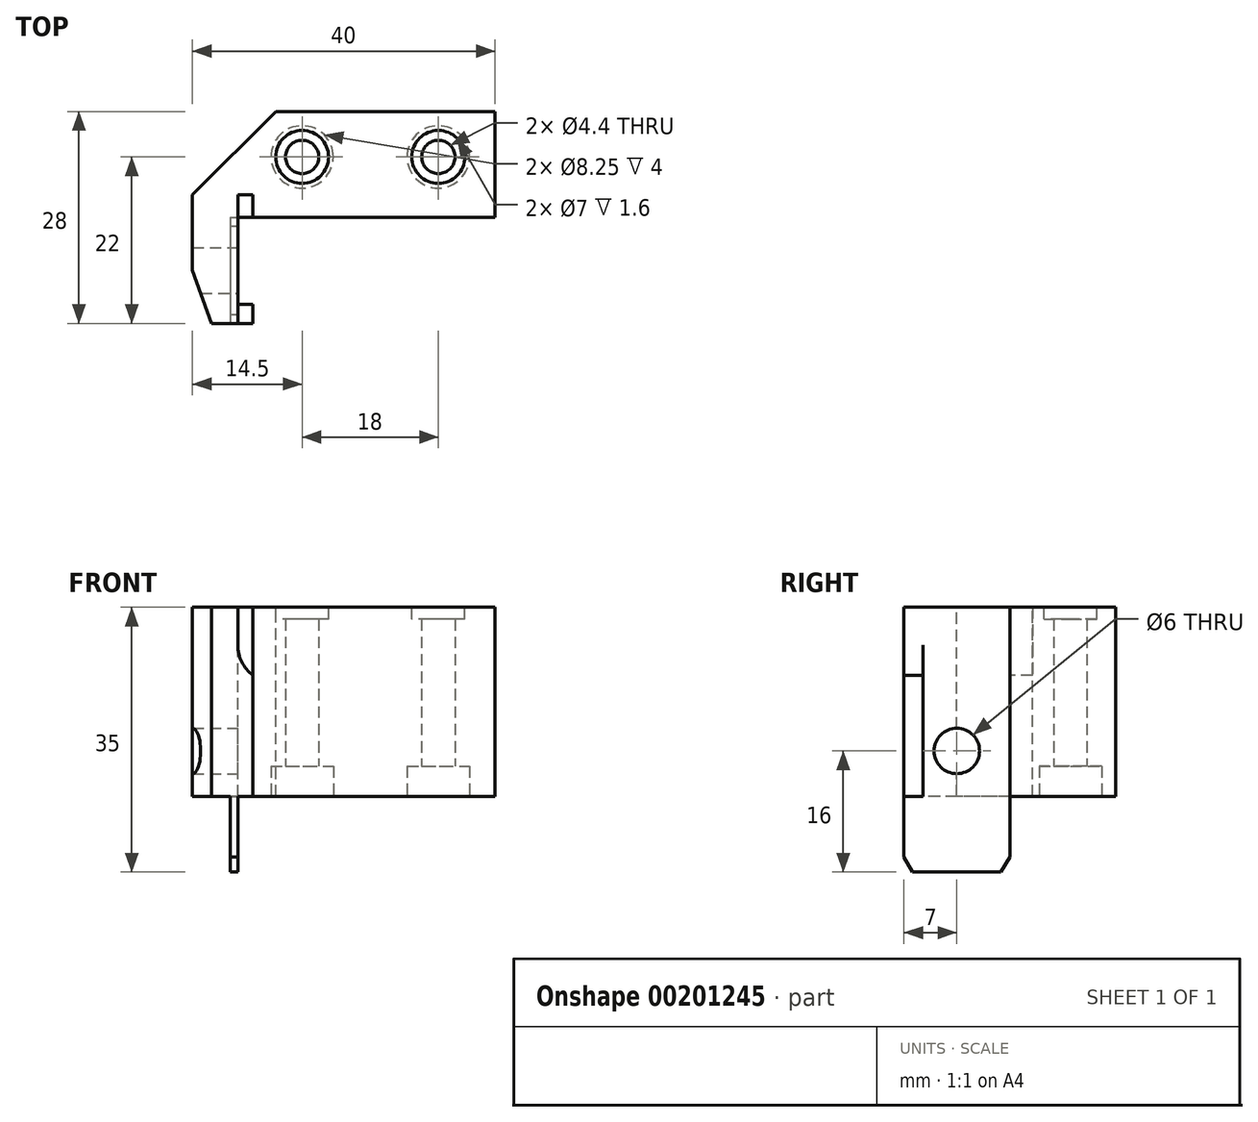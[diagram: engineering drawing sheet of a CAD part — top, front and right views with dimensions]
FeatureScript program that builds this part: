
annotation { "Feature Type Name" : "Feature", "Feature Type Description" : "" }
export const myFeature = defineFeature(function(context is Context, id is Id, definition is map)
    precondition{}
    {
        {
            var Q0;
            Q0=qCreatedBy(makeId("Top.planeOp"),FACE);
            var sketch = newSketch(context, id + "F0", { "sketchPlane" : qUnion([Q0])});
            skLineSegment(sketch, "E0", {"start": v(0, 14) * mm, "end": v(0, 28) * mm});
            skLineSegment(sketch, "E1", {"start": v(0, 28) * mm, "end": v(-29, 28) * mm});
            skLineSegment(sketch, "E2", {"start": v(-29, 28) * mm, "end": v(-40, 17) * mm});
            skLineSegment(sketch, "E3", {"start": v(-40, 17) * mm, "end": v(-40, 7) * mm});
            skLineSegment(sketch, "E4", {"start": v(-40, 7) * mm, "end": v(-37.45, 0) * mm});
            skLineSegment(sketch, "E5", {"start": v(-37.45, 0) * mm, "end": v(-32, 0) * mm});
            skLineSegment(sketch, "E6", {"start": v(-32, 0) * mm, "end": v(-32, 2.5) * mm});
            skLineSegment(sketch, "E7", {"start": v(-32, 2.5) * mm, "end": v(-34, 2.5) * mm});
            skLineSegment(sketch, "E8", {"start": v(-34, 2.5) * mm, "end": v(-34, 14) * mm});
            skLineSegment(sketch, "E9", {"start": v(-34, 14) * mm, "end": v(0, 14) * mm});
            skLineSegment(sketch, "E10", {"start": v(0, 22) * mm, "end": v(-35, 22) * mm, "construction": true});
            skLineSegment(sketch, "E11", {"start": v(-7.5, 28) * mm, "end": v(-7.5, 14) * mm, "construction": true});
            skLineSegment(sketch, "E12", {"start": v(-25.5, 14) * mm, "end": v(-25.5, 28) * mm, "construction": true});
            skPoint(sketch, "E13", {"position": v(-25.5, 22) * mm});
            skPoint(sketch, "E14", {"position": v(-7.5, 22) * mm});
            skSolve(sketch);
        }
        {
            var Q0;
            Q0=makeQuery(id+"F0.imprint","IMPRINT",FACE,{"disambiguationData":[TD([[makeQuery(id+"F0.imprint","IMPRINT",EDGE,{"derivedFrom":sQuery(id+"F0.wireOp",EDGE,"E0")}),1.0]])]});
            extrude(context, id + "F1", {"entities" : qUnion([Q0]), "oppositeDirection" : true, "depth" : 35 * mm});
        }
        {
            var Q0;
            Q0=makeQuery(id+"F1.opExtrude","SWEPT_FACE",FACE,{"disambiguationData":[OSD([sQuery(id+"F0.wireOp",EDGE,"E5")])]});
            var sketch = newSketch(context, id + "F2", { "sketchPlane" : qUnion([Q0])});
            skLineSegment(sketch, "E15.0", {"start": v(-34, 0) * mm, "end": v(0, 0) * mm});
            skLineSegment(sketch, "E16.0", {"start": v(0, -35) * mm, "end": v(0, 0) * mm});
            skLineSegment(sketch, "E17.0", {"start": v(-34, -35) * mm, "end": v(0, -35) * mm});
            skLineSegment(sketch, "E18.0", {"start": v(-37.45, -35) * mm, "end": v(-32, -35) * mm});
            skLineSegment(sketch, "E19.0", {"start": v(-40, -35) * mm, "end": v(-37.45, -35) * mm});
            skLineSegment(sketch, "E20.0", {"start": v(-40, -35) * mm, "end": v(-40, 0) * mm});
            skLineSegment(sketch, "E21.0", {"start": v(-40, 0) * mm, "end": v(-37.45, 0) * mm});
            skLineSegment(sketch, "E22.0", {"start": v(-37.45, 0) * mm, "end": v(-32, 0) * mm});
            skLineSegment(sketch, "E23.0", {"start": v(-32, -35) * mm, "end": v(-32, 0) * mm});
            skLineSegment(sketch, "E24.0", {"start": v(-37.45, -35) * mm, "end": v(-37.45, 0) * mm});
            skLineSegment(sketch, "E25", {"start": v(-34, 0) * mm, "end": v(-34, -5) * mm});
            skLineSegment(sketch, "E26", {"start": v(-29, -10) * mm, "end": v(0, -10) * mm});
            skLineSegment(sketch, "E27", {"start": v(-40, -25) * mm, "end": v(-35, -25) * mm});
            skLineSegment(sketch, "E28", {"start": v(-35, -25) * mm, "end": v(-35, -35) * mm});
            skLineSegment(sketch, "E29", {"start": v(0, -25) * mm, "end": v(-34, -25) * mm});
            skLineSegment(sketch, "E30", {"start": v(-34, -25) * mm, "end": v(-34, -35) * mm});
            skPoint(sketch, "E31.visualSharp", {"position": v(-34, -10) * mm});
            skArc(sketch, "E31.filletArc", {"start": v(-34, -5) * mm, "mid": v(-32.54, -8.54) * mm, "end": v(-29, -10) * mm});
            skSolve(sketch);
        }
        {
            var Q0;
            {var subQ2=sQuery(id+"F2.wireOp",EDGE,"E15.0");Q0=makeQuery(id+"F2.imprint","IMPRINT",FACE,{"disambiguationData":[TD([[makeQuery(id+"F2.imprint","IMPRINT",EDGE,{"derivedFrom":subQ2}),-1.0]])]});}
            var Q1;
            {var subQ3=sQuery(id+"F2.wireOp",EDGE,"E25");Q1=makeQuery(id+"F2.imprint","IMPRINT",FACE,{"disambiguationData":[TD([[makeQuery(id+"F2.imprint","IMPRINT",EDGE,{"derivedFrom":subQ3}),1.0]])]});}
            extrude(context, id + "F3", {"entities" : qUnion([Q0, Q1]), "operationType" : NewBodyOperationType.REMOVE, "oppositeDirection" : true, "depth" : 17 * mm});
        }
        {
            var Q0;
            {var subQ3=sQuery(id+"F2.wireOp",EDGE,"E28");Q0=makeQuery(id+"F2.imprint","IMPRINT",FACE,{"disambiguationData":[TD([[makeQuery(id+"F2.imprint","IMPRINT",EDGE,{"derivedFrom":subQ3}),-1.0]])]});}
            var Q1;
            {var subQ0=sQuery(id+"F2.wireOp",EDGE,"E19.0");Q1=makeQuery(id+"F2.imprint","IMPRINT",FACE,{"disambiguationData":[TD([[makeQuery(id+"F2.imprint","IMPRINT",EDGE,{"derivedFrom":subQ0}),1.0]])]});}
            var Q2;
            {var subQ0=sQuery(id+"F2.wireOp",EDGE,"E17.0");Q2=makeQuery(id+"F2.imprint","IMPRINT",FACE,{"disambiguationData":[TD([[makeQuery(id+"F2.imprint","IMPRINT",EDGE,{"derivedFrom":subQ0}),1.0]])]});}
            extrude(context, id + "F4", {"entities" : qUnion([Q0, Q1, Q2]), "operationType" : NewBodyOperationType.REMOVE, "endBound" : BoundingType.THROUGH_ALL, "oppositeDirection" : true, "depth" : 25 * mm});
        }
        {
            var Q0;
            Q0=makeQuery(id+"F1.opExtrude","SWEPT_FACE",FACE,{"disambiguationData":[OSD([sQuery(id+"F0.wireOp",EDGE,"E1")])]});
            var sketch = newSketch(context, id + "F5", { "sketchPlane" : qUnion([Q0])});
            skLineSegment(sketch, "E32.0", {"start": v(0, -25) * mm, "end": v(34, -25) * mm});
            skLineSegment(sketch, "E33.0", {"start": v(34, -25) * mm, "end": v(34, -35) * mm});
            skLineSegment(sketch, "E34.0", {"start": v(37.45, -35) * mm, "end": v(32, -35) * mm});
            skLineSegment(sketch, "E35.0", {"start": v(32, -35) * mm, "end": v(32, 0) * mm});
            skLineSegment(sketch, "E36.0", {"start": v(35, -25) * mm, "end": v(35, -35) * mm});
            skLineSegment(sketch, "E37.0", {"start": v(40, -25) * mm, "end": v(35, -25) * mm});
            skLineSegment(sketch, "E38.0", {"start": v(40, -35) * mm, "end": v(40, 0) * mm});
            skLineSegment(sketch, "E39.0", {"start": v(37.45, 0) * mm, "end": v(32, 0) * mm});
            skLineSegment(sketch, "E40.0", {"start": v(40, 0) * mm, "end": v(37.45, 0) * mm});
            skLineSegment(sketch, "E41.0", {"start": v(40, -35) * mm, "end": v(37.45, -35) * mm});
            skLineSegment(sketch, "E42", {"start": v(34, -25) * mm, "end": v(35, -25) * mm});
            skSolve(sketch);
        }
        {
            var Q0;
            {var subQ0=sQuery(id+"F5.wireOp",EDGE,"E33.0");Q0=makeQuery(id+"F5.imprint","IMPRINT",FACE,{"disambiguationData":[TD([[makeQuery(id+"F5.imprint","IMPRINT",EDGE,{"derivedFrom":subQ0}),-1.0]])]});}
            var Q1;
            Q1=makeQuery(id+"F1.opExtrude","SWEPT_FACE",FACE,{"disambiguationData":[OSD([sQuery(id+"F0.wireOp",EDGE,"E9")])]});
            extrude(context, id + "F6", {"entities" : qUnion([Q0]), "operationType" : NewBodyOperationType.REMOVE, "endBound" : BoundingType.UP_TO_SURFACE, "oppositeDirection" : true, "endBoundEntityFace" : qUnion([Q1]), "depth" : 25 * mm});
        }
        {
            var Q0;
            Q0=makeQuery(id+"F1.opExtrude","SWEPT_FACE",FACE,{"disambiguationData":[OSD([sQuery(id+"F0.wireOp",EDGE,"E0")])]});
            var sketch = newSketch(context, id + "F7", { "sketchPlane" : qUnion([Q0])});
            skLineSegment(sketch, "E43.0.0", {"start": v(17, 0) * mm, "end": v(0, 0) * mm});
            skLineSegment(sketch, "E43.0.1", {"start": v(0, 0) * mm, "end": v(0, -5) * mm});
            skLineSegment(sketch, "E43.0.2", {"start": v(0, -5) * mm, "end": v(2.5, -5) * mm});
            skLineSegment(sketch, "E43.0.3", {"start": v(2.5, -5) * mm, "end": v(2.5, -35) * mm});
            skLineSegment(sketch, "E43.0.4", {"start": v(2.5, -35) * mm, "end": v(23, -35) * mm});
            skLineSegment(sketch, "E43.0.5", {"start": v(23, -35) * mm, "end": v(23, -25) * mm});
            skLineSegment(sketch, "E43.0.6", {"start": v(23, -25) * mm, "end": v(14, -25) * mm});
            skLineSegment(sketch, "E43.0.7", {"start": v(14, -25) * mm, "end": v(14, -5) * mm});
            skLineSegment(sketch, "E43.0.8", {"start": v(14, -5) * mm, "end": v(17, -5) * mm});
            skLineSegment(sketch, "E43.0.9", {"start": v(17, -5) * mm, "end": v(17, 0) * mm});
            skLineSegment(sketch, "E44.0.0", {"start": v(0, -9) * mm, "end": v(2.5, -9) * mm});
            skLineSegment(sketch, "E44.0.1", {"start": v(0, -9) * mm, "end": v(0, -35) * mm});
            skLineSegment(sketch, "E44.0.2", {"start": v(0, -35) * mm, "end": v(2.5, -35) * mm});
            skLineSegment(sketch, "E44.0.3", {"start": v(2.5, -35) * mm, "end": v(2.5, -9) * mm});
            skLineSegment(sketch, "E45.0.1", {"start": v(2.5, -9) * mm, "end": v(2.5, -5) * mm});
            skLineSegment(sketch, "E45.0.2", {"start": v(2.5, -5) * mm, "end": v(0, -5) * mm});
            skLineSegment(sketch, "E45.0.3", {"start": v(0, -5) * mm, "end": v(0, -9) * mm});
            skLineSegment(sketch, "E46.0.0", {"start": v(14, -5) * mm, "end": v(14, -10) * mm});
            skLineSegment(sketch, "E46.0.1", {"start": v(14, -10) * mm, "end": v(17, -10) * mm});
            skLineSegment(sketch, "E46.0.2", {"start": v(17, -10) * mm, "end": v(17, -5) * mm});
            skLineSegment(sketch, "E46.0.3", {"start": v(17, -5) * mm, "end": v(14, -5) * mm});
            skLineSegment(sketch, "E47", {"start": v(14, -25) * mm, "end": v(14, -35) * mm});
            skCircle(sketch, "E48", {"center": v(7, -19) * mm, "radius": 3 * mm});
            skLineSegment(sketch, "E49", {"start": v(0, -33) * mm, "end": v(1.15, -35) * mm});
            skLineSegment(sketch, "E50", {"start": v(12.85, -35) * mm, "end": v(14, -33) * mm});
            skSolve(sketch);
        }
        {
            var Q0;
            {var subQ0=sQuery(id+"F7.wireOp",EDGE,"E43.0.5");Q0=makeQuery(id+"F7.imprint","IMPRINT",FACE,{"disambiguationData":[TD([[makeQuery(id+"F7.imprint","IMPRINT",EDGE,{"derivedFrom":subQ0}),1.0]])]});}
            var Q1;
            {var subQ3=sQuery(id+"F7.wireOp",EDGE,"E50");Q1=makeQuery(id+"F7.imprint","IMPRINT",FACE,{"disambiguationData":[TD([[makeQuery(id+"F7.imprint","IMPRINT",EDGE,{"derivedFrom":subQ3}),-1.0]])]});}
            var Q2;
            Q2=makeQuery(id+"F7.imprint","IMPRINT",FACE,{"disambiguationData":[TD([[makeQuery(id+"F7.imprint","IMPRINT",EDGE,{"derivedFrom":sQuery(id+"F7.wireOp",EDGE,"E48")}),1.0]])]});
            var Q3;
            {var subQ3=sQuery(id+"F7.wireOp",EDGE,"E49");Q3=makeQuery(id+"F7.imprint","IMPRINT",FACE,{"disambiguationData":[TD([[makeQuery(id+"F7.imprint","IMPRINT",EDGE,{"derivedFrom":subQ3}),-1.0]])]});}
            extrude(context, id + "F8", {"entities" : qUnion([Q0, Q1, Q2, Q3]), "operationType" : NewBodyOperationType.REMOVE, "endBound" : BoundingType.THROUGH_ALL, "oppositeDirection" : true, "depth" : 25 * mm});
        }
        {
            var Q0;
            Q0=makeQuery(id+"F8.boolean.opBoolean","MERGE",FACE,{"derivedFrom":[makeQuery(id+"F4.boolean.opBoolean","COPY",FACE,{"derivedFrom":makeQuery(id+"F4.opExtrude","SWEPT_FACE",FACE,{"disambiguationData":[OSD([sQuery(id+"F2.wireOp",EDGE,"E27")])]})}),makeQuery(id+"F6.boolean.opBoolean","MERGE",FACE,{"derivedFrom":[makeQuery(id+"F4.boolean.opBoolean","COPY",FACE,{"derivedFrom":makeQuery(id+"F4.opExtrude","SWEPT_FACE",FACE,{"disambiguationData":[OSD([sQuery(id+"F2.wireOp",EDGE,"E29")])]})}),makeQuery(id+"F6.opExtrude","SWEPT_FACE",FACE,{"disambiguationData":[OSD([sQuery(id+"F5.wireOp",EDGE,"E32.0")])]})]}),makeQuery(id+"F8.opExtrude","SWEPT_FACE",FACE,{"disambiguationData":[OSD([sQuery(id+"F7.wireOp",EDGE,"E43.0.6")])]})]});
            var sketch = newSketch(context, id + "F9", { "sketchPlane" : qUnion([Q0])});
            skLineSegment(sketch, "E51.0", {"start": v(0, -22) * mm, "end": v(-35, -22) * mm, "construction": true});
            skLineSegment(sketch, "E52.0", {"start": v(-25.5, -14) * mm, "end": v(-25.5, -28) * mm, "construction": true});
            skLineSegment(sketch, "E53.0", {"start": v(-7.5, -28) * mm, "end": v(-7.5, -14) * mm, "construction": true});
            skPoint(sketch, "E54.0", {"position": v(-25.5, -22) * mm});
            skPoint(sketch, "E55.0", {"position": v(-7.5, -22) * mm});
            skSolve(sketch);
        }
        {
            var Q0;
            Q0=sQuery(id+"F9.wireOp",VERTEX,"E54.0");
            var Q1;
            Q1=sQuery(id+"F9.wireOp",VERTEX,"E55.0");
            var Q2;
            Q2=makeQuery(id+"F1.opExtrude","SWEPT_BODY",BODY,{"disambiguationData":[OSD([sQuery(id+"F0.wireOp",EDGE,"E0"),sQuery(id+"F0.wireOp",EDGE,"E1"),sQuery(id+"F0.wireOp",EDGE,"E2"),sQuery(id+"F0.wireOp",EDGE,"E3"),sQuery(id+"F0.wireOp",EDGE,"E4"),sQuery(id+"F0.wireOp",EDGE,"E5"),sQuery(id+"F0.wireOp",EDGE,"E6"),sQuery(id+"F0.wireOp",EDGE,"E7"),sQuery(id+"F0.wireOp",EDGE,"E8"),sQuery(id+"F0.wireOp",EDGE,"E9")])]});
            hole(context, id + "F10", {"style" : HoleStyle.C_BORE, "endStyle" : HoleEndStyle.THROUGH, "standardTappedOrClearance" : lookupTablePath({ "standard" : "ISO", "fit" : "Normal", "size" : "M4", "type" : "Clearance" }), "standardBlindInLast" : lookupTablePath({ "fit" : "Standard", "standard" : "ISO", "size" : "M4", "type" : "Clearance" }), "holeDiameter" : 4.4 * mm, "cBoreDiameter" : 8.25 * mm, "cBoreDepth" : 4 * mm, "startFromSketch" : true, "locations" : qUnion([Q0, Q1]), "scope" : qUnion([Q2]), "isTappedThrough" : true});
        }
        {
            var Q0;
            Q0=makeQuery(id+"F0.imprint","IMPRINT",FACE,{"disambiguationData":[TD([[makeQuery(id+"F0.imprint","IMPRINT",EDGE,{"derivedFrom":sQuery(id+"F0.wireOp",EDGE,"E0")}),1.0]])]});
            var sketch = newSketch(context, id + "F11", { "sketchPlane" : qUnion([Q0])});
            skLineSegment(sketch, "E56.0", {"start": v(0, 22) * mm, "end": v(-35, 22) * mm, "construction": true});
            skLineSegment(sketch, "E57.0", {"start": v(-25.5, 14) * mm, "end": v(-25.5, 28) * mm, "construction": true});
            skLineSegment(sketch, "E58.0", {"start": v(-7.5, 28) * mm, "end": v(-7.5, 14) * mm, "construction": true});
            skPoint(sketch, "E59.0", {"position": v(-25.5, 22) * mm});
            skPoint(sketch, "E60.0", {"position": v(-7.5, 22) * mm});
            skCircle(sketch, "E61", {"center": v(-25.5, 22) * mm, "radius": 3.5 * mm});
            skCircle(sketch, "E62", {"center": v(-7.5, 22) * mm, "radius": 3.5 * mm});
            skCircle(sketch, "E63.0", {"center": v(-25.5, 22) * mm, "radius": 2.2 * mm});
            skCircle(sketch, "E64.0", {"center": v(-7.5, 22) * mm, "radius": 2.2 * mm});
            skSolve(sketch);
        }
        {
            var Q0;
            Q0=makeQuery(id+"F11.imprint","IMPRINT",FACE,{"disambiguationData":[TD([[makeQuery(id+"F11.imprint","IMPRINT",EDGE,{"derivedFrom":sQuery(id+"F11.wireOp",EDGE,"E61")}),1.0]])]});
            var Q1;
            Q1=makeQuery(id+"F11.imprint","IMPRINT",FACE,{"disambiguationData":[TD([[makeQuery(id+"F11.imprint","IMPRINT",EDGE,{"derivedFrom":sQuery(id+"F11.wireOp",EDGE,"E62")}),1.0]])]});
            extrude(context, id + "F12", {"entities" : qUnion([Q0, Q1]), "operationType" : NewBodyOperationType.REMOVE, "oppositeDirection" : true, "depth" : 1.6 * mm});
        }
    });
